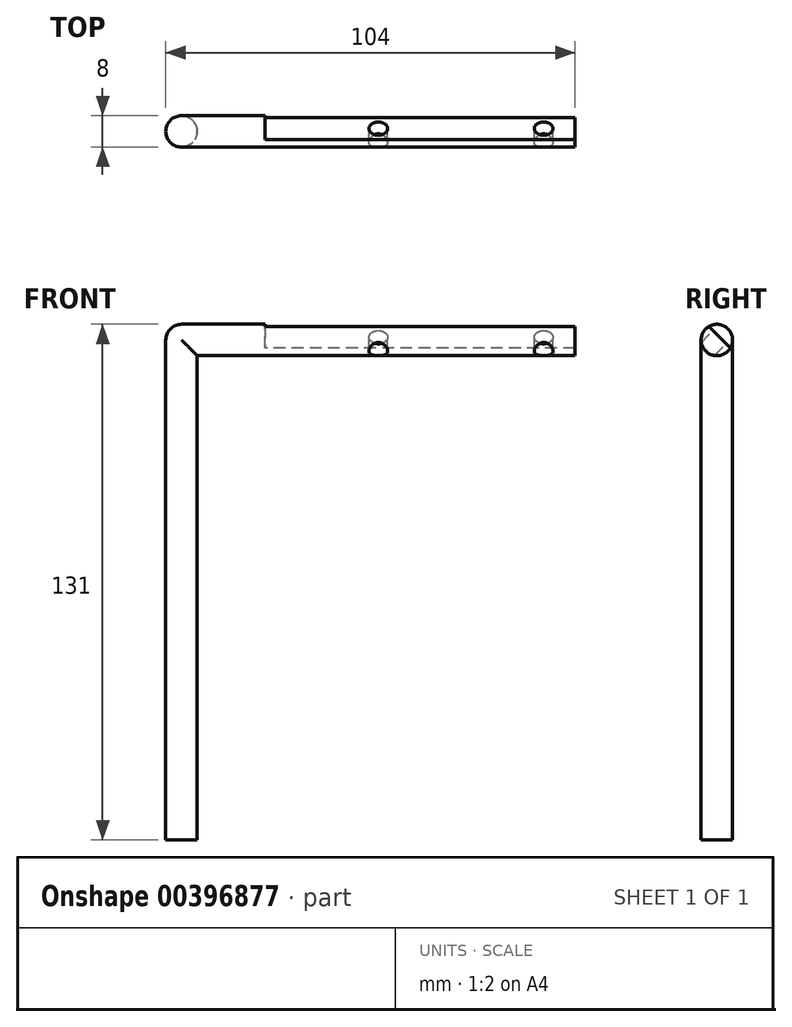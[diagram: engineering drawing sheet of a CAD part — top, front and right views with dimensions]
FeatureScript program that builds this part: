
annotation { "Feature Type Name" : "Feature", "Feature Type Description" : "" }
export const myFeature = defineFeature(function(context is Context, id is Id, definition is map)
    precondition{}
    {
        {
            var Q0;
            Q0=qCreatedBy(makeId("Top.planeOp"),FACE);
            var sketch = newSketch(context, id + "F0", { "sketchPlane" : qUnion([Q0])});
            skLineSegment(sketch, "E0.bottom", {"start": v(0, 0) * mm, "end": v(100, 0) * mm});
            skLineSegment(sketch, "E0.top", {"start": v(0, 4) * mm, "end": v(100, 4) * mm});
            skLineSegment(sketch, "E0.left", {"start": v(0, 0) * mm, "end": v(0, 4) * mm});
            skLineSegment(sketch, "E0.right", {"start": v(100, 0) * mm, "end": v(100, 4) * mm});
            skCircle(sketch, "E1", {"center": v(100, 0) * mm, "radius": 4 * mm});
            skSolve(sketch);
        }
        {
            var Q0;
            {var subQ4=sQuery(id+"F0.wireOp",EDGE,"E0.top");Q0=makeQuery(id+"F0.imprint","IMPRINT",FACE,{"disambiguationData":[TD([[makeQuery(id+"F0.imprint","IMPRINT",EDGE,{"derivedFrom":subQ4}),-1.0]])]});}
            var Q1;
            Q1=sQuery(id+"F0.wireOp",EDGE,"E0.bottom");
            revolve(context, id + "F1", {"entities" : qUnion([Q0]), "axis" : qUnion([Q1]), "revolveType" : RevolveType.ONE_DIRECTION, "angle" : 360 * degree});
        }
        {
            var Q0;
            {var subQ0=sQuery(id+"F0.wireOp",EDGE,"E0.right");Q0=makeQuery(id+"F0.imprint","IMPRINT",FACE,{"disambiguationData":[TD([[makeQuery(id+"F0.imprint","IMPRINT",EDGE,{"derivedFrom":subQ0}),-1.0]])]});}
            var Q1;
            {var subQ0=sQuery(id+"F0.wireOp",EDGE,"E0.right");Q1=makeQuery(id+"F0.imprint","IMPRINT",FACE,{"disambiguationData":[TD([[makeQuery(id+"F0.imprint","IMPRINT",EDGE,{"derivedFrom":subQ0}),1.0]])]});}
            extrude(context, id + "F2", {"entities" : qUnion([Q0, Q1]), "operationType" : NewBodyOperationType.ADD, "oppositeDirection" : true, "depth" : 135 * mm, "offsetDistance" : 25 * mm});
        }
        {
            var Q0;
            Q0=makeQuery(id+"F2.opExtrude","CAP_FACE",FACE,{"disambiguationData":[OSD([sQuery(id+"F0.wireOp",EDGE,"E1")])],"isStart":true});
            var sketch = newSketch(context, id + "F3", { "sketchPlane" : qUnion([Q0])});
            skLineSegment(sketch, "E2", {"start": v(100, 4) * mm, "end": v(100, -4) * mm});
            skSolve(sketch);
        }
        {
            var Q0;
            Q0=makeQuery(id+"F3.imprint","IMPRINT",FACE,{"disambiguationData":[TD([[makeQuery(id+"F3.imprint","IMPRINT",EDGE,{"derivedFrom":sQuery(id+"F3.wireOp",EDGE,"E2")}),1.0]])]});
            var Q1;
            Q1=sQuery(id+"F3.wireOp",EDGE,"E2");
            revolve(context, id + "F4", {"operationType" : NewBodyOperationType.ADD, "entities" : qUnion([Q0]), "axis" : qUnion([Q1]), "revolveType" : RevolveType.FULL});
        }
        {
            var Q0;
            Q0=qCreatedBy(makeId("Top.planeOp"),FACE);
            var Q1;
            {var subQ0=makeQuery(id+"F1.opRevolve","SWEPT_FACE",FACE,{"disambiguationData":[OSD([sQuery(id+"F0.wireOp",EDGE,"E0.top")])]});Q1=makeQuery(id+"FGNPgHpNrWebPq1_1.boolean.opBoolean","MERGE",FACE,{"derivedFrom":[subQ0,makeQuery(id+"FGNPgHpNrWebPq1_1.opPattern","COPY",FACE,{"derivedFrom":subQ0,"instanceName":"1"})]});}
            cPlane(context, id + "F5", {"entities" : qUnion([Q0, Q1]), "cplaneType" : CPlaneType.LINE_ANGLE, "offset" : 25 * mm, "angle" : 45 * degree, "width" : 150 * mm, "height" : 150 * mm});
        }
        {
            var Q0;
            Q0=qCreatedBy(id+"F5.planeOp",FACE);
            cPlane(context, id + "F6", {"entities" : qUnion([Q0]), "cplaneType" : CPlaneType.OFFSET, "offset" : 4 * mm, "oppositeDirection" : true, "width" : 150 * mm, "height" : 150 * mm});
        }
        {
            var Q0;
            Q0=qCreatedBy(id+"F6.planeOp",FACE);
            var sketch = newSketch(context, id + "F7", { "sketchPlane" : qUnion([Q0])});
            skLineSegment(sketch, "E3.bottom", {"start": v(78.81, 6.26) * mm, "end": v(-78.81, 6.26) * mm});
            skLineSegment(sketch, "E3.top", {"start": v(78.81, -6.26) * mm, "end": v(-78.81, -6.26) * mm});
            skLineSegment(sketch, "E3.left", {"start": v(78.81, 6.26) * mm, "end": v(78.81, -6.26) * mm});
            skLineSegment(sketch, "E3.right", {"start": v(-78.81, 6.26) * mm, "end": v(-78.81, -6.26) * mm});
            skPoint(sketch, "E3.middle", {"position": v(0, 0) * mm});
            skLineSegment(sketch, "E4", {"start": v(0, 0) * mm, "end": v(8, 0) * mm, "construction": true});
            skLineSegment(sketch, "E5", {"start": v(0, 0) * mm, "end": v(-25, 0) * mm, "construction": true});
            skCircle(sketch, "E6", {"center": v(8, 0) * mm, "radius": 2.38 * mm});
            skCircle(sketch, "E7", {"center": v(-25, 0) * mm, "radius": 3.09 * mm});
            skLineSegment(sketch, "E8", {"start": v(0, 0) * mm, "end": v(50, 0) * mm, "construction": true});
            skCircle(sketch, "E9", {"center": v(50, 0) * mm, "radius": 2.38 * mm});
            skSolve(sketch);
        }
        {
            var Q0;
            Q0=makeQuery(id+"F7.imprint","IMPRINT",FACE,{"disambiguationData":[TD([[makeQuery(id+"F7.imprint","IMPRINT",EDGE,{"derivedFrom":sQuery(id+"F7.wireOp",EDGE,"E3.bottom")}),1.0]])]});
            var Q1;
            Q1=makeQuery(id+"F7.imprint","IMPRINT",FACE,{"disambiguationData":[TD([[makeQuery(id+"F7.imprint","IMPRINT",EDGE,{"derivedFrom":sQuery(id+"F7.wireOp",EDGE,"E6")}),1.0]])]});
            var Q2;
            Q2=makeQuery(id+"F7.imprint","IMPRINT",FACE,{"disambiguationData":[TD([[makeQuery(id+"F7.imprint","IMPRINT",EDGE,{"derivedFrom":sQuery(id+"F7.wireOp",EDGE,"E7")}),1.0]])]});
            extrude(context, id + "F8", {"entities" : qUnion([Q0, Q1, Q2]), "operationType" : NewBodyOperationType.REMOVE, "depth" : 3 * mm, "offsetDistance" : 25 * mm});
        }
        {
            var Q0;
            Q0=makeQuery(id+"F7.imprint","IMPRINT",FACE,{"disambiguationData":[TD([[makeQuery(id+"F7.imprint","IMPRINT",EDGE,{"derivedFrom":sQuery(id+"F7.wireOp",EDGE,"E7")}),1.0]])]});
            var Q1;
            Q1=makeQuery(id+"F7.imprint","IMPRINT",FACE,{"disambiguationData":[TD([[makeQuery(id+"F7.imprint","IMPRINT",EDGE,{"derivedFrom":sQuery(id+"F7.wireOp",EDGE,"E6")}),1.0]])]});
            var Q2;
            Q2=makeQuery(id+"F7.imprint","IMPRINT",FACE,{"disambiguationData":[TD([[makeQuery(id+"F7.imprint","IMPRINT",EDGE,{"derivedFrom":sQuery(id+"F7.wireOp",EDGE,"E9")}),1.0]])]});
            extrude(context, id + "F9", {"entities" : qUnion([Q0, Q1, Q2]), "operationType" : NewBodyOperationType.REMOVE, "depth" : 25 * mm, "offsetDistance" : 25 * mm});
        }
        {
            var Q0;
            Q0=makeQuery(id+"F1.opRevolve","SWEPT_BODY",BODY,{"disambiguationData":[OSD([sQuery(id+"F0.wireOp",EDGE,"E0.bottom"),sQuery(id+"F0.wireOp",EDGE,"E0.top"),sQuery(id+"F0.wireOp",EDGE,"E0.left"),sQuery(id+"F0.wireOp",EDGE,"E1")])]});
            var Q1;
            Q1=qCreatedBy(makeId("Right.planeOp"),FACE);
            mirror(context, id + "F10", {"operationType" : NewBodyOperationType.ADD, "entities" : qUnion([Q0]), "mirrorPlane" : qUnion([Q1])});
        }
        {
            var Q0;
            Q0=qCreatedBy(id+"F6.planeOp",FACE);
            var sketch = newSketch(context, id + "F11", { "sketchPlane" : qUnion([Q0])});
            skLineSegment(sketch, "E10.bottom", {"start": v(0, 0) * mm, "end": v(150.08, 0) * mm});
            skLineSegment(sketch, "E10.top", {"start": v(0, -114.14) * mm, "end": v(150.08, -114.14) * mm});
            skLineSegment(sketch, "E10.left", {"start": v(0, 0) * mm, "end": v(0, -114.14) * mm});
            skLineSegment(sketch, "E10.right", {"start": v(150.08, 0) * mm, "end": v(150.08, -114.14) * mm});
            skLineSegment(sketch, "E11.MirrorCS", {"start": v(0, 114.14) * mm, "end": v(150.08, 114.14) * mm});
            skLineSegment(sketch, "E12.MirrorCS", {"start": v(150.08, 0) * mm, "end": v(150.08, 114.14) * mm});
            skLineSegment(sketch, "E13.MirrorCS", {"start": v(0, 0) * mm, "end": v(0, 114.14) * mm});
            skSolve(sketch);
        }
        {
            var Q0;
            Q0=makeQuery(id+"F11.imprint","IMPRINT",FACE,{"disambiguationData":[TD([[makeQuery(id+"F11.imprint","IMPRINT",EDGE,{"derivedFrom":sQuery(id+"F11.wireOp",EDGE,"E10.bottom")}),-1.0]])]});
            var Q1;
            Q1=makeQuery(id+"F11.imprint","IMPRINT",FACE,{"disambiguationData":[TD([[makeQuery(id+"F11.imprint","IMPRINT",EDGE,{"derivedFrom":sQuery(id+"F11.wireOp",EDGE,"E10.bottom")}),1.0]])]});
            extrude(context, id + "F12", {"entities" : qUnion([Q0, Q1]), "operationType" : NewBodyOperationType.REMOVE, "depth" : 115 * mm, "offsetDistance" : 25 * mm});
        }
        {
            var Q0;
            Q0=makeQuery(id+"F10.opPattern","COPY",FACE,{"derivedFrom":makeQuery(id+"F2.opExtrude","CAP_FACE",FACE,{"disambiguationData":[OSD([sQuery(id+"F0.wireOp",EDGE,"E1")])],"isStart":false}),"instanceName":"1"});
            var sketch = newSketch(context, id + "F13", { "sketchPlane" : qUnion([Q0])});
            skLineSegment(sketch, "E14.bottom", {"start": v(-116.75, -4.65) * mm, "end": v(-79.9, -4.65) * mm});
            skLineSegment(sketch, "E14.top", {"start": v(-116.75, 13) * mm, "end": v(-79.9, 13) * mm});
            skLineSegment(sketch, "E14.left", {"start": v(-116.75, -4.65) * mm, "end": v(-116.75, 13) * mm});
            skLineSegment(sketch, "E14.right", {"start": v(-79.9, -4.65) * mm, "end": v(-79.9, 13) * mm});
            skSolve(sketch);
        }
        {
            var Q0;
            Q0=makeQuery(id+"F13.imprint","IMPRINT",FACE,{"disambiguationData":[TD([[makeQuery(id+"F13.imprint","IMPRINT",EDGE,{"derivedFrom":sQuery(id+"F13.wireOp",EDGE,"E14.bottom")}),1.0]])]});
            var Q1;
            Q1=makeQuery(id+"F13.imprint","IMPRINT",FACE,{"disambiguationData":[TD([[makeQuery(id+"F13.imprint","IMPRINT",EDGE,{"derivedFrom":makeQuery(id+"F10.opPattern","COPY",EDGE,{"derivedFrom":makeQuery(id+"F2.opExtrude","CAP_EDGE",EDGE,{"disambiguationData":[OSD([sQuery(id+"F0.wireOp",EDGE,"E1")])],"isStart":false}),"instanceName":"1"})}),1.0]])]});
            extrude(context, id + "F14", {"entities" : qUnion([Q0, Q1]), "operationType" : NewBodyOperationType.REMOVE, "oppositeDirection" : true, "depth" : 8 * mm, "offsetDistance" : 25 * mm});
        }
    });
